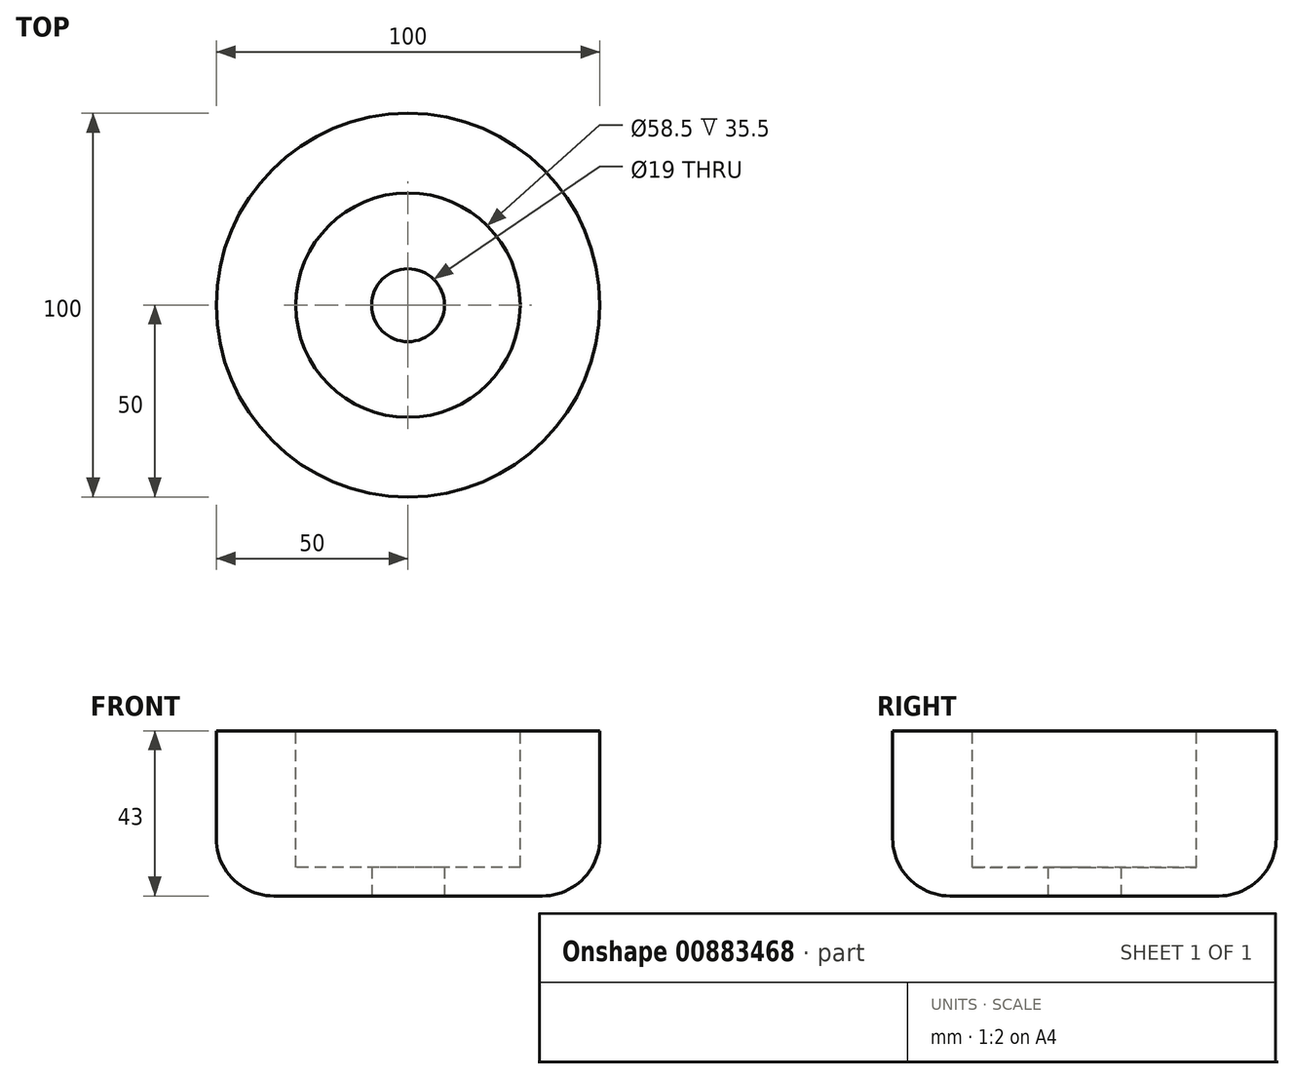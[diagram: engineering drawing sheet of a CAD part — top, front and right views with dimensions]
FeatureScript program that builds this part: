
annotation { "Feature Type Name" : "Feature", "Feature Type Description" : "" }
export const myFeature = defineFeature(function(context is Context, id is Id, definition is map)
    precondition{}
    {
        {
            var Q0;
            Q0=qCreatedBy(makeId("Top.planeOp"),FACE);
            var sketch = newSketch(context, id + "F0", { "sketchPlane" : qUnion([Q0])});
            skCircle(sketch, "E0", {"center": v(0, 0) * mm, "radius": 50 * mm});
            skSolve(sketch);
        }
        {
            var Q0;
            Q0=makeQuery(id+"F0.imprint","IMPRINT",FACE,{"disambiguationData":[TD([[makeQuery(id+"F0.imprint","IMPRINT",EDGE,{"derivedFrom":sQuery(id+"F0.wireOp",EDGE,"E0")}),1.0]])]});
            extrude(context, id + "F1", {"entities" : qUnion([Q0]), "depth" : 43 * mm, "offsetDistance" : 25 * mm});
        }
        {
            var Q0;
            Q0=makeQuery(id+"F1.opExtrude","CAP_FACE",FACE,{"disambiguationData":[OSD([sQuery(id+"F0.wireOp",EDGE,"E0")])],"isStart":false});
            var sketch = newSketch(context, id + "F2", { "sketchPlane" : qUnion([Q0])});
            skCircle(sketch, "E1", {"center": v(0, 0) * mm, "radius": 29.25 * mm});
            skSolve(sketch);
        }
        {
            var Q0;
            Q0 = qSketchRegion(id + "F2", true);
            extrude(context, id + "F3", {"entities" : qUnion([Q0]), "operationType" : NewBodyOperationType.REMOVE, "depth" : -35.5 * mm, "offsetDistance" : 25 * mm});
        }
        {
            var Q0;
            Q0=makeQuery(id+"F1.opExtrude","CAP_EDGE",EDGE,{"disambiguationData":[OSD([sQuery(id+"F0.wireOp",EDGE,"E0")])],"isStart":true});
            fillet(context, id + "F4", {"entities" : qUnion([Q0]), "radius" : 15 * mm, "tangentPropagation" : true, "allowEdgeOverflow" : false});
        }
        {
            var Q0;
            Q0=makeQuery(id+"F1.opExtrude","CAP_FACE",FACE,{"disambiguationData":[OSD([sQuery(id+"F0.wireOp",EDGE,"E0")])],"isStart":true});
            var sketch = newSketch(context, id + "F5", { "sketchPlane" : qUnion([Q0])});
            skCircle(sketch, "E2", {"center": v(0, 0) * mm, "radius": 9.5 * mm});
            skSolve(sketch);
        }
        {
            var Q0;
            Q0=makeQuery(id+"F5.imprint","IMPRINT",FACE,{"disambiguationData":[TD([[makeQuery(id+"F5.imprint","IMPRINT",EDGE,{"derivedFrom":sQuery(id+"F5.wireOp",EDGE,"E2")}),1.0]])]});
            extrude(context, id + "F6", {"entities" : qUnion([Q0]), "operationType" : NewBodyOperationType.REMOVE, "depth" : -8 * mm, "offsetDistance" : 25 * mm});
        }
    });
